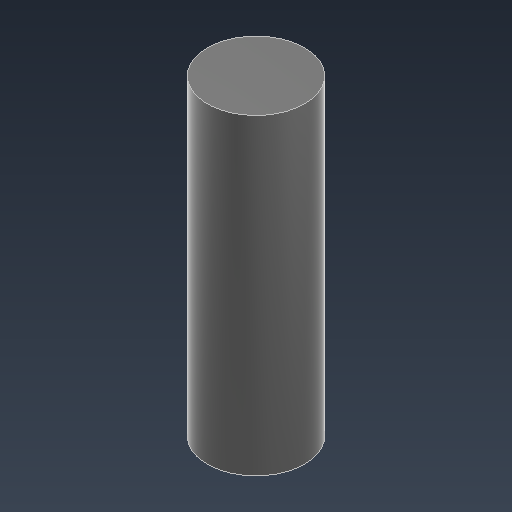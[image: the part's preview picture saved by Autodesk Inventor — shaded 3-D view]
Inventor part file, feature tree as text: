
AUTODESK INVENTOR PART (.ipt)
format: ipt  version: 2021.3 (Build 253353000, 353)  size: 92,160 bytes
history: native  units: mm
features: extrude x1, sketch x1
ambient origin geometry x8: Origin, YZ Plane, XZ Plane, XY Plane, X Axis, Y Axis, Z Axis, Center Point
bodies: Solid1 (feature_tree)
feature tree (2):
  extrude  "Extrusion1"  Depth=12.2mm TaperAngle=0.0deg
  sketch  "Sketch1"  dims[d0=3.8mm d1=12.2mm d2=0.0mm]
